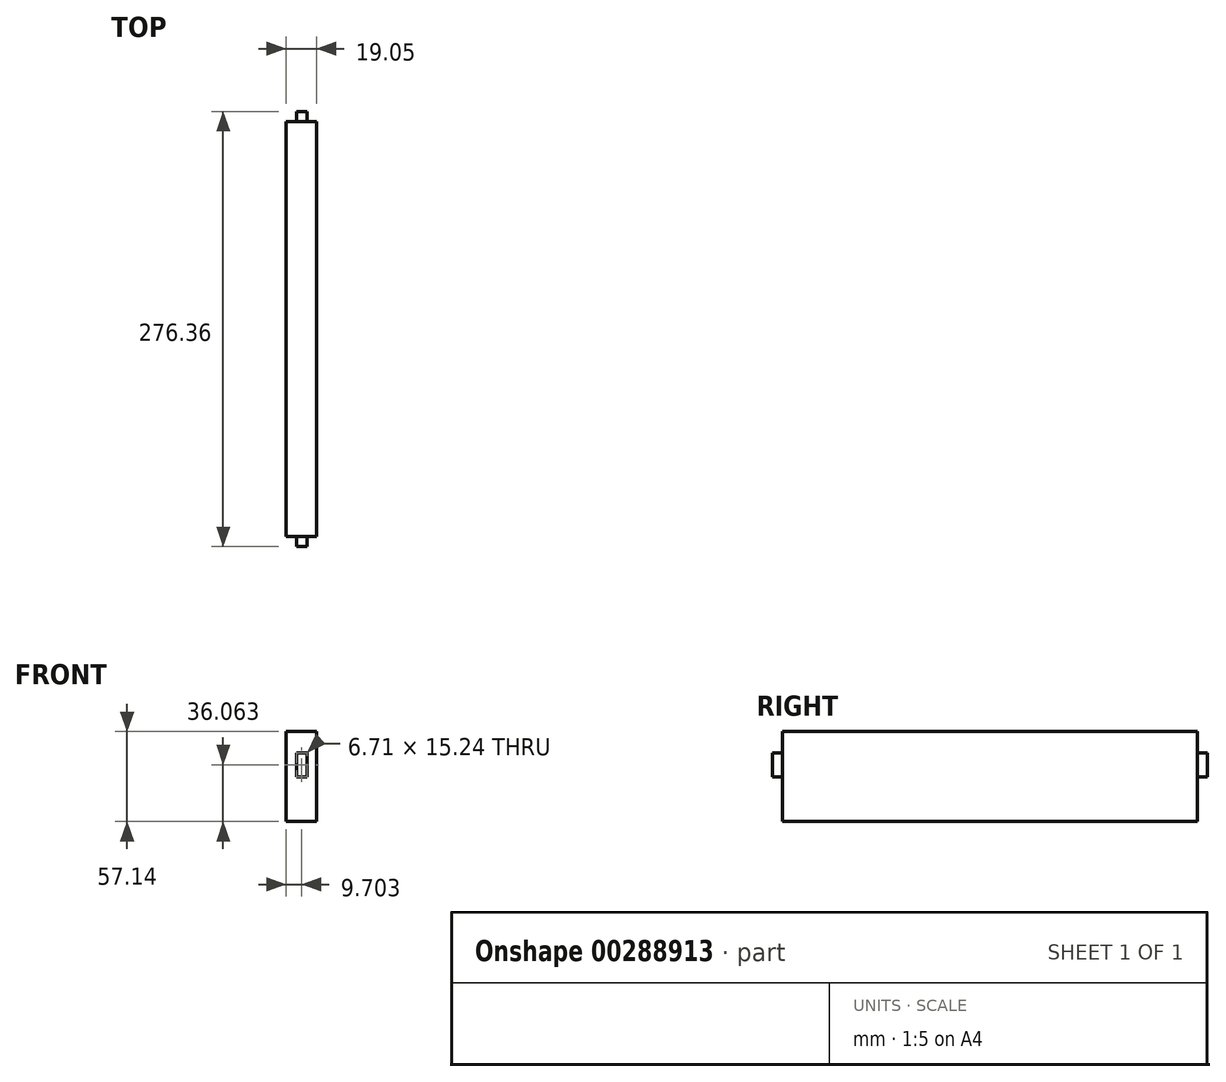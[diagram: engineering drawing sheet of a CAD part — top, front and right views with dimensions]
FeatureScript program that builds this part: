
annotation { "Feature Type Name" : "Feature", "Feature Type Description" : "" }
export const myFeature = defineFeature(function(context is Context, id is Id, definition is map)
    precondition{}
    {
        {
            var Q0;
            Q0=qCreatedBy(makeId("Right.planeOp"),FACE);
            var sketch = newSketch(context, id + "F0", { "sketchPlane" : qUnion([Q0])});
            skLineSegment(sketch, "E0.bottom", {"start": v(-131.83, 28.58) * mm, "end": v(131.83, 28.58) * mm});
            skLineSegment(sketch, "E0.top", {"start": v(-131.83, -28.58) * mm, "end": v(131.83, -28.58) * mm});
            skLineSegment(sketch, "E0.left", {"start": v(-131.83, 28.58) * mm, "end": v(-131.83, -28.58) * mm});
            skLineSegment(sketch, "E0.right", {"start": v(131.83, 28.58) * mm, "end": v(131.83, -28.58) * mm});
            skPoint(sketch, "E0.middle", {"position": v(0, 0) * mm});
            skSolve(sketch);
        }
        {
            var Q0;
            Q0 = qSketchRegion(id + "F0", true);
            extrude(context, id + "F1", {"entities" : qUnion([Q0]), "depth" : 19.05 * mm});
        }
        {
            var Q0;
            Q0=makeQuery(id+"F1.opExtrude","SWEPT_FACE",FACE,{"disambiguationData":[OSD([sQuery(id+"F0.wireOp",EDGE,"E0.left")])]});
            var sketch = newSketch(context, id + "F2", { "sketchPlane" : qUnion([Q0])});
            skLineSegment(sketch, "E1", {"start": v(0, 15.11) * mm, "end": v(19.05, 15.11) * mm, "construction": true});
            skLineSegment(sketch, "E2", {"start": v(9.53, 28.57) * mm, "end": v(9.53, -28.58) * mm, "construction": true});
            skLineSegment(sketch, "E3", {"start": v(0, -0.13) * mm, "end": v(19.05, -0.13) * mm, "construction": true});
            skLineSegment(sketch, "E4", {"start": v(6.35, 15.11) * mm, "end": v(6.35, -0.13) * mm});
            skLineSegment(sketch, "E5", {"start": v(6.35, -0.13) * mm, "end": v(13.06, -0.13) * mm});
            skLineSegment(sketch, "E6", {"start": v(13.06, -0.13) * mm, "end": v(13.06, 15.11) * mm});
            skLineSegment(sketch, "E7", {"start": v(13.06, 15.11) * mm, "end": v(6.35, 15.11) * mm});
            skSolve(sketch);
        }
        {
            var Q0;
            Q0 = qSketchRegion(id + "F2", true);
            extrude(context, id + "F3", {"entities" : qUnion([Q0]), "operationType" : NewBodyOperationType.ADD, "depth" : 6.35 * mm});
        }
        {
            var Q0;
            Q0=makeQuery(id+"F1.opExtrude","SWEPT_FACE",FACE,{"disambiguationData":[OSD([sQuery(id+"F0.wireOp",EDGE,"E0.right")])]});
            var sketch = newSketch(context, id + "F4", { "sketchPlane" : qUnion([Q0])});
            skLineSegment(sketch, "E8", {"start": v(-9.53, 28.58) * mm, "end": v(-9.53, -28.57) * mm, "construction": true});
            skLineSegment(sketch, "E9", {"start": v(-19.05, 15.11) * mm, "end": v(0, 15.11) * mm, "construction": true});
            skLineSegment(sketch, "E10", {"start": v(-9.53, 15.11) * mm, "end": v(-13.06, 15.11) * mm});
            skLineSegment(sketch, "E11", {"start": v(-13.06, 15.11) * mm, "end": v(-13.06, -0.13) * mm});
            skLineSegment(sketch, "E12", {"start": v(-13.06, -0.13) * mm, "end": v(-6.35, -0.13) * mm});
            skLineSegment(sketch, "E13", {"start": v(-6.35, -0.13) * mm, "end": v(-6.35, 15.11) * mm});
            skLineSegment(sketch, "E14", {"start": v(-6.35, 15.11) * mm, "end": v(-13.06, 15.11) * mm});
            skSolve(sketch);
        }
        {
            var Q0;
            Q0 = qSketchRegion(id + "F4", true);
            extrude(context, id + "F5", {"entities" : qUnion([Q0]), "operationType" : NewBodyOperationType.ADD, "depth" : 6.35 * mm});
        }
    });
